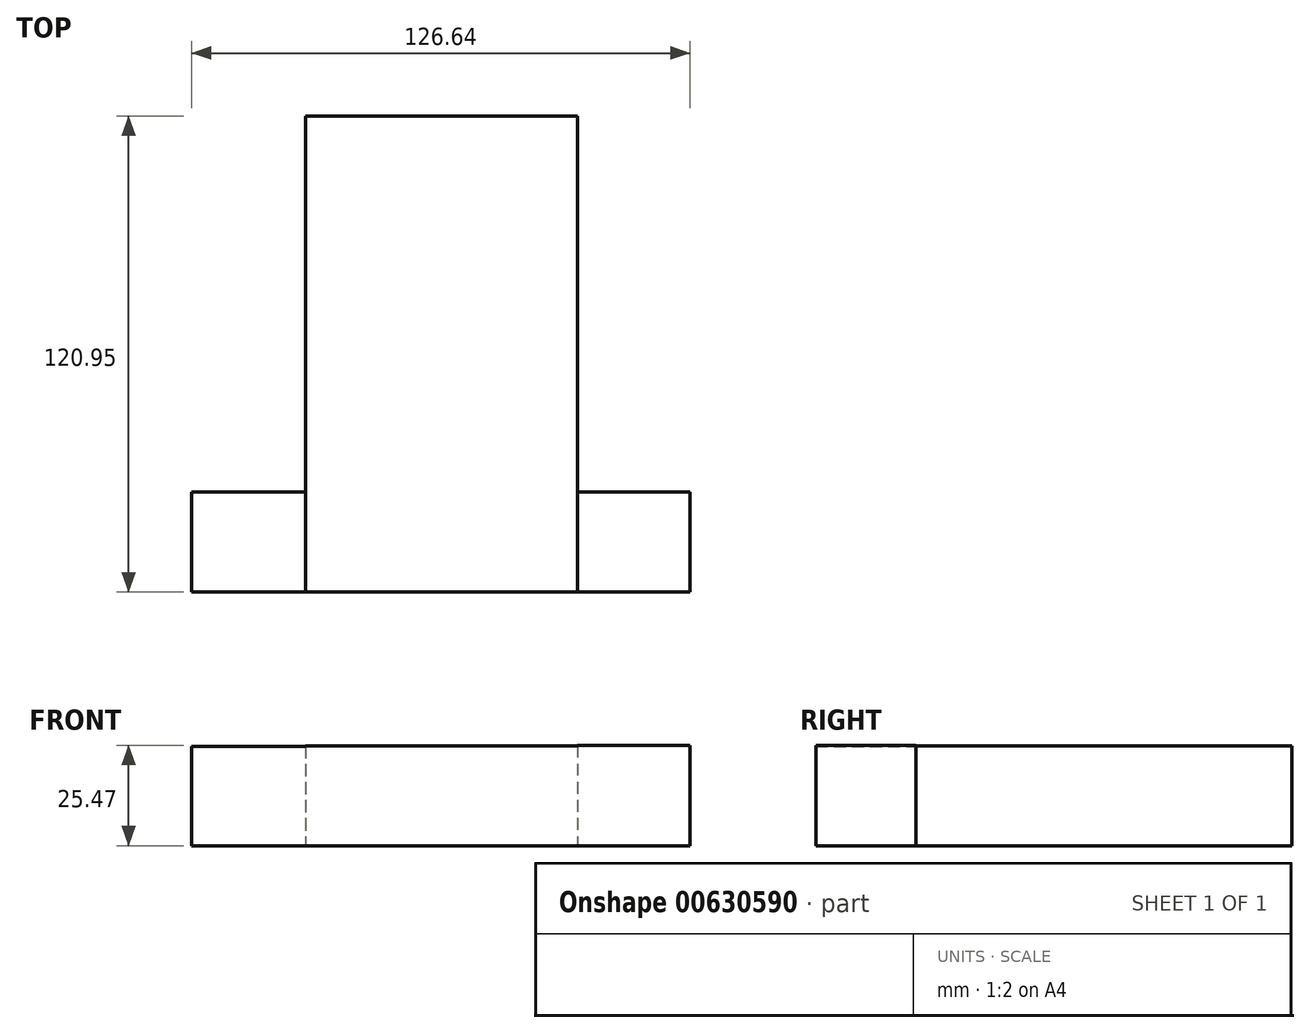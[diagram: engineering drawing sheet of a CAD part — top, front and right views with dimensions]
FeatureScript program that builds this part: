
annotation { "Feature Type Name" : "Feature", "Feature Type Description" : "" }
export const myFeature = defineFeature(function(context is Context, id is Id, definition is map)
    precondition{}
    {
        {
            var Q0;
            Q0=qCreatedBy(makeId("Top.planeOp"),FACE);
            var sketch = newSketch(context, id + "F0", { "sketchPlane" : qUnion([Q0])});
            skLineSegment(sketch, "E0.bottom", {"start": v(-34.4, 47.63) * mm, "end": v(34.68, 47.63) * mm});
            skLineSegment(sketch, "E0.top", {"start": v(-34.4, -47.92) * mm, "end": v(34.68, -47.92) * mm});
            skLineSegment(sketch, "E0.left", {"start": v(-34.4, 47.63) * mm, "end": v(-34.4, -47.92) * mm});
            skLineSegment(sketch, "E0.right", {"start": v(34.68, 47.63) * mm, "end": v(34.68, -47.92) * mm});
            skSolve(sketch);
        }
        {
            var Q0;
            Q0=makeQuery(id+"F0.imprint","IMPRINT",FACE,{"disambiguationData":[TD([[makeQuery(id+"F0.imprint","IMPRINT",EDGE,{"derivedFrom":sQuery(id+"F0.wireOp",EDGE,"E0.bottom")}),-1.0]])]});
            extrude(context, id + "F1", {"entities" : qUnion([Q0]), "depth" : 25.4 * mm, "offsetDistance" : 25.4 * mm});
        }
        {
            var Q0;
            Q0=makeQuery(id+"F1.opExtrude","SWEPT_FACE",FACE,{"disambiguationData":[OSD([sQuery(id+"F0.wireOp",EDGE,"E0.top")])]});
            var sketch = newSketch(context, id + "F2", { "sketchPlane" : qUnion([Q0])});
            skLineSegment(sketch, "E1.bottom", {"start": v(34.68, 0) * mm, "end": v(63.28, 0) * mm});
            skLineSegment(sketch, "E1.top", {"start": v(34.68, 25.47) * mm, "end": v(63.28, 25.47) * mm});
            skLineSegment(sketch, "E1.left", {"start": v(34.68, 0) * mm, "end": v(34.68, 25.47) * mm});
            skLineSegment(sketch, "E1.right", {"start": v(63.28, 0) * mm, "end": v(63.28, 25.47) * mm});
            skLineSegment(sketch, "E2.bottom", {"start": v(-34.4, 0) * mm, "end": v(-63.36, 0) * mm});
            skLineSegment(sketch, "E2.top", {"start": v(-34.4, 25.2) * mm, "end": v(-63.36, 25.2) * mm});
            skLineSegment(sketch, "E2.left", {"start": v(-34.4, 0) * mm, "end": v(-34.4, 25.2) * mm});
            skLineSegment(sketch, "E2.right", {"start": v(-63.36, 0) * mm, "end": v(-63.36, 25.2) * mm});
            skSolve(sketch);
        }
        {
            var Q0;
            Q0=qSketchRegion(id+"F2",true);
            var Q1;
            {var subQ4=sQuery(id+"F2.wireOp",EDGE,"E2.left");Q1=makeQuery(id+"F2.imprint","IMPRINT",FACE,{"disambiguationData":[TD([[makeQuery(id+"F2.imprint","IMPRINT",EDGE,{"derivedFrom":subQ4}),1.0]])]});}
            extrude(context, id + "F3", {"entities" : qUnion([Q0, Q1]), "operationType" : NewBodyOperationType.ADD, "depth" : 25.4 * mm, "offsetDistance" : 25.4 * mm});
        }
    });
